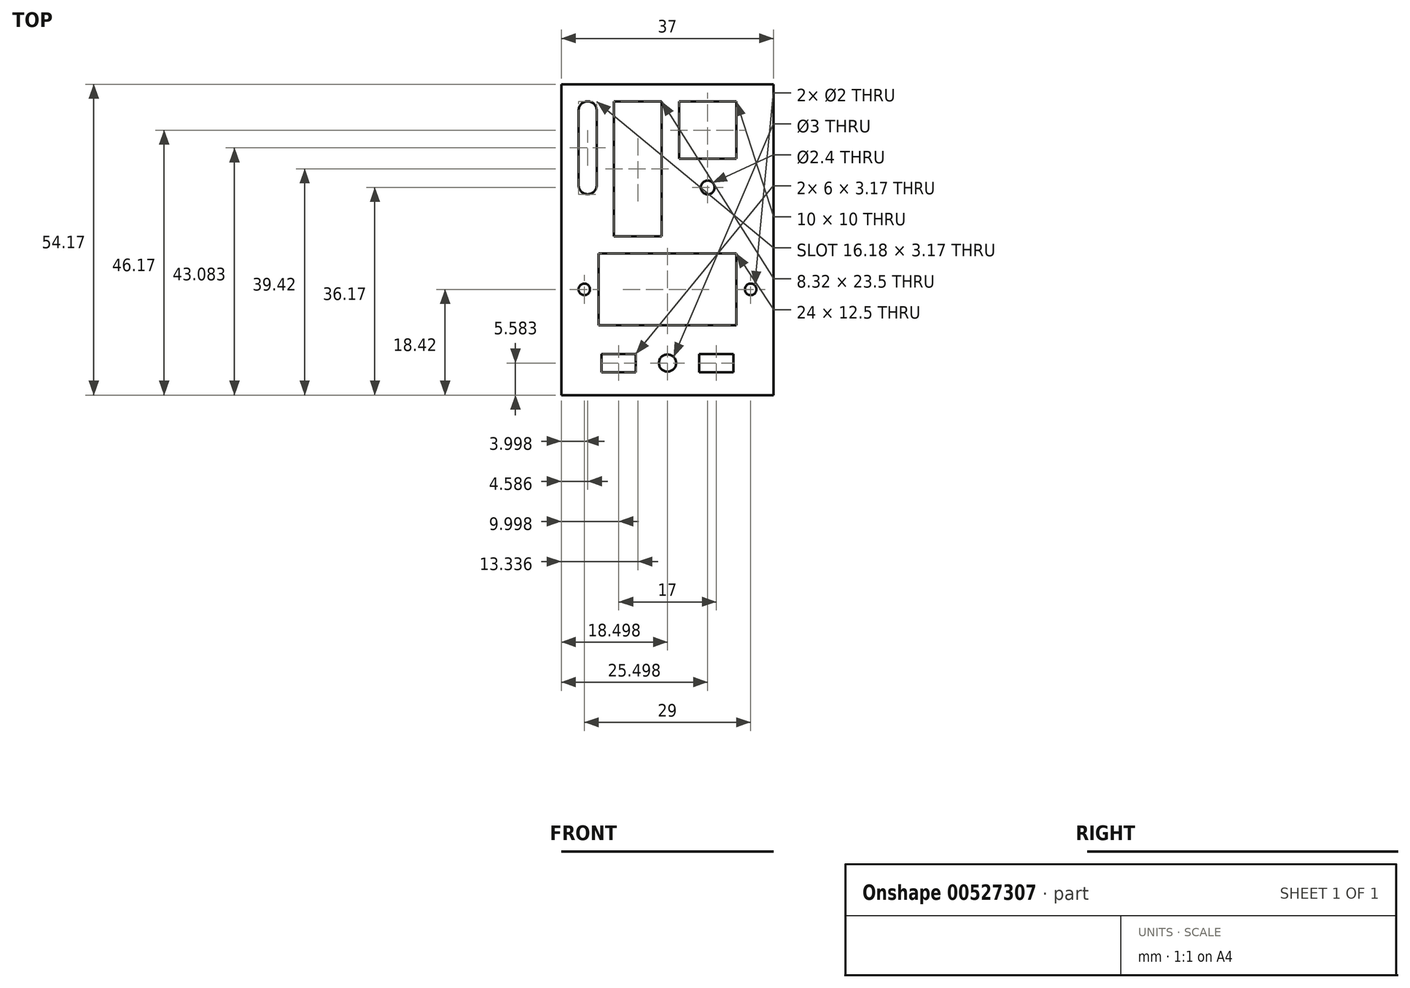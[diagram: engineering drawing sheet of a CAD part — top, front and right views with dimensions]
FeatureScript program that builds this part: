
annotation { "Feature Type Name" : "Feature", "Feature Type Description" : "" }
export const myFeature = defineFeature(function(context is Context, id is Id, definition is map)
    precondition{}
    {
        {
            var Q0;
            Q0=qCreatedBy(makeId("Top.planeOp"),FACE);
            var sketch = newSketch(context, id + "F0", { "sketchPlane" : qUnion([Q0])});
            skLineSegment(sketch, "E0.bottom", {"start": v(-4.8, -6.85) * mm, "end": v(32.2, -6.85) * mm});
            skLineSegment(sketch, "E0.top", {"start": v(-4.8, 47.32) * mm, "end": v(32.2, 47.32) * mm});
            skLineSegment(sketch, "E0.left", {"start": v(-4.8, -6.85) * mm, "end": v(-4.8, 47.32) * mm});
            skLineSegment(sketch, "E0.right", {"start": v(32.2, -6.85) * mm, "end": v(32.2, 47.32) * mm});
            skLineSegment(sketch, "E1.bottom", {"start": v(15.7, 34.32) * mm, "end": v(25.7, 34.32) * mm});
            skLineSegment(sketch, "E1.top", {"start": v(15.7, 24.32) * mm, "end": v(25.7, 24.32) * mm});
            skLineSegment(sketch, "E1.left", {"start": v(15.7, 34.32) * mm, "end": v(15.7, 24.32) * mm});
            skLineSegment(sketch, "E1.right", {"start": v(25.7, 34.32) * mm, "end": v(25.7, 24.32) * mm});
            skPoint(sketch, "E1.middle", {"position": v(20.7, 29.32) * mm});
            skLineSegment(sketch, "E2.top", {"start": v(15.7, 44.32) * mm, "end": v(25.7, 44.32) * mm});
            skLineSegment(sketch, "E2.left", {"start": v(15.7, 34.32) * mm, "end": v(15.7, 44.32) * mm});
            skLineSegment(sketch, "E2.right", {"start": v(25.7, 34.32) * mm, "end": v(25.7, 44.32) * mm});
            skCircle(sketch, "E3", {"center": v(20.7, 29.32) * mm, "radius": 1.2 * mm});
            skLineSegment(sketch, "E4.bottom", {"start": v(1.7, 17.82) * mm, "end": v(25.7, 17.82) * mm});
            skLineSegment(sketch, "E4.top", {"start": v(1.7, 5.32) * mm, "end": v(25.7, 5.32) * mm});
            skLineSegment(sketch, "E4.left", {"start": v(1.7, 17.82) * mm, "end": v(1.7, 5.32) * mm});
            skLineSegment(sketch, "E4.right", {"start": v(25.7, 17.82) * mm, "end": v(25.7, 5.32) * mm});
            skPoint(sketch, "E4.middle", {"position": v(13.7, 11.57) * mm});
            skCircle(sketch, "E5", {"center": v(28.2, 11.57) * mm, "radius": 1 * mm});
            skLineSegment(sketch, "E6", {"start": v(13.7, 11.57) * mm, "end": v(13.7, 17.82) * mm});
            skCircle(sketch, "E7.MirrorC", {"center": v(-0.8, 11.57) * mm, "radius": 1 * mm});
            skCircle(sketch, "E8", {"center": v(13.7, -1.27) * mm, "radius": 1.5 * mm});
            skLineSegment(sketch, "E9.bottom", {"start": v(2.2, 0.32) * mm, "end": v(8.2, 0.32) * mm});
            skLineSegment(sketch, "E9.top", {"start": v(2.2, -2.85) * mm, "end": v(8.2, -2.85) * mm});
            skLineSegment(sketch, "E9.left", {"start": v(2.2, 0.32) * mm, "end": v(2.2, -2.85) * mm});
            skLineSegment(sketch, "E9.right", {"start": v(8.2, 0.32) * mm, "end": v(8.2, -2.85) * mm});
            skPoint(sketch, "E9.middle", {"position": v(5.2, -1.27) * mm});
            skLineSegment(sketch, "E10", {"start": v(13.7, -1.27) * mm, "end": v(13.7, 0.23) * mm});
            skLineSegment(sketch, "E11.MirrorCS", {"start": v(19.2, 0.32) * mm, "end": v(19.2, -2.85) * mm});
            skLineSegment(sketch, "E12.MirrorCS", {"start": v(25.2, 0.32) * mm, "end": v(19.2, 0.32) * mm});
            skLineSegment(sketch, "E13.MirrorCS", {"start": v(25.2, 0.32) * mm, "end": v(25.2, -2.85) * mm});
            skLineSegment(sketch, "E14.MirrorCS", {"start": v(25.2, -2.85) * mm, "end": v(19.2, -2.85) * mm});
            skCircle(sketch, "E15", {"center": v(-0.21, 42.73) * mm, "radius": 1.59 * mm});
            skCircle(sketch, "E16", {"center": v(-0.21, 29.73) * mm, "radius": 1.59 * mm});
            skLineSegment(sketch, "E17", {"start": v(-1.8, 42.73) * mm, "end": v(-1.8, 29.73) * mm});
            skLineSegment(sketch, "E18", {"start": v(-0.21, 42.73) * mm, "end": v(-0.21, 29.73) * mm});
            skLineSegment(sketch, "E19.MirrorCS", {"start": v(1.37, 42.73) * mm, "end": v(1.37, 29.73) * mm});
            skLineSegment(sketch, "E20.bottom", {"start": v(12.7, 44.32) * mm, "end": v(4.37, 44.32) * mm});
            skLineSegment(sketch, "E20.top", {"start": v(12.7, 20.82) * mm, "end": v(4.37, 20.82) * mm});
            skLineSegment(sketch, "E20.left", {"start": v(12.7, 44.32) * mm, "end": v(12.7, 20.82) * mm});
            skLineSegment(sketch, "E20.right", {"start": v(4.37, 44.32) * mm, "end": v(4.37, 20.82) * mm});
            skSolve(sketch);
        }
        {
            var Q0;
            {var subQ3=sQuery(id+"F0.wireOp",EDGE,"wtiJx0A3-Piaz-BVb3-eG2h-1XG7ABVZoibs.bottom");Q0=makeQuery(id+"F0.imprint","IMPRINT",FACE,{"disambiguationData":[TD([[makeQuery(id+"F0.imprint","IMPRINT",EDGE,{"derivedFrom":subQ3}),1.0]])]});}
            var Q1;
            Q1=makeQuery(id+"F0.imprint","IMPRINT",FACE,{"disambiguationData":[TD([[makeQuery(id+"F0.imprint","IMPRINT",EDGE,{"derivedFrom":sQuery(id+"F0.wireOp",EDGE,"E1.top")}),1.0]])]});
            var Q2;
            Q2=makeQuery(id+"F0.imprint","IMPRINT",FACE,{"disambiguationData":[TD([[makeQuery(id+"F0.imprint","IMPRINT",EDGE,{"derivedFrom":sQuery(id+"F0.wireOp",EDGE,"E0.bottom")}),1.0]])]});
            extrude(context, id + "F1", {"entities" : qUnion([Q0, Q1, Q2]), "depth" : 1 / 203.2 * mm, "offsetDistance" : 25 * mm});
        }
    });
